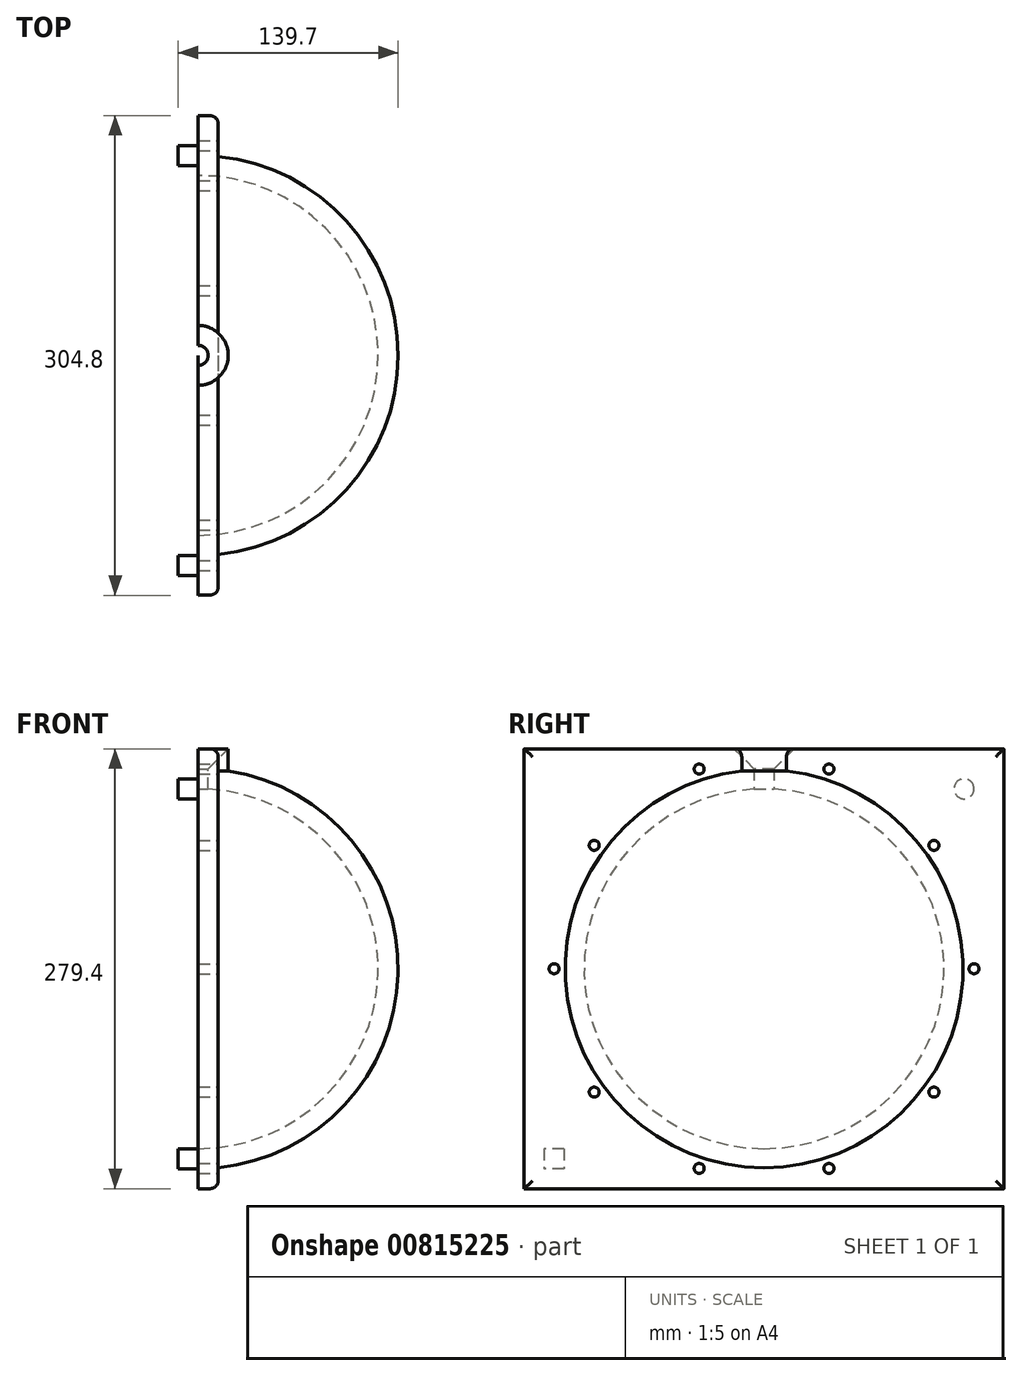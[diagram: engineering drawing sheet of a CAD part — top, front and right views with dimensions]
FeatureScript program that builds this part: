
annotation { "Feature Type Name" : "Feature", "Feature Type Description" : "" }
export const myFeature = defineFeature(function(context is Context, id is Id, definition is map)
    precondition{}
    {
        {
            var Q0;
            Q0=qCreatedBy(makeId("Right.planeOp"),FACE);
            var sketch = newSketch(context, id + "F0", { "sketchPlane" : qUnion([Q0])});
            skCircle(sketch, "E0", {"center": v(0, 0) * mm, "radius": 114.3 * mm});
            skLineSegment(sketch, "E1", {"start": v(0, -114.3) * mm, "end": v(0, -139.7) * mm});
            skLineSegment(sketch, "E2", {"start": v(0, -139.7) * mm, "end": v(152.4, -139.7) * mm});
            skLineSegment(sketch, "E3", {"start": v(152.4, -139.7) * mm, "end": v(152.4, 139.7) * mm});
            skLineSegment(sketch, "E4", {"start": v(152.4, 139.7) * mm, "end": v(6.35, 139.7) * mm});
            skLineSegment(sketch, "E5", {"start": v(6.35, 139.7) * mm, "end": v(6.35, 114.12) * mm});
            skSolve(sketch);
        }
        {
            var Q0;
            {var subQ0=sQuery(id+"F0.wireOp",EDGE,"E1");Q0=makeQuery(id+"F0.imprint","IMPRINT",FACE,{"disambiguationData":[TD([[makeQuery(id+"F0.imprint","IMPRINT",EDGE,{"derivedFrom":subQ0}),1.0]])]});}
            var Q1;
            Q1=sQuery(id+"F0.wireOp",EDGE,"E1");
            revolve(context, id + "F1", {"surfaceOperationType" : NewSurfaceOperationType.NEW, "entities" : qUnion([Q0]), "axis" : qUnion([Q1]), "revolveType" : RevolveType.ONE_DIRECTION, "angle" : 180 * degree});
        }
        {
            var Q0;
            Q0=makeQuery(id+"F1.opRevolve","CAP_FACE",FACE,{"disambiguationData":[OSD([sQuery(id+"F0.wireOp",EDGE,"E0"),sQuery(id+"F0.wireOp",EDGE,"E1"),sQuery(id+"F0.wireOp",EDGE,"E2"),sQuery(id+"F0.wireOp",EDGE,"E3"),sQuery(id+"F0.wireOp",EDGE,"E4"),sQuery(id+"F0.wireOp",EDGE,"E5")])],"isStart":false});
            var sketch = newSketch(context, id + "F2", { "sketchPlane" : qUnion([Q0])});
            skCircle(sketch, "E6", {"center": v(-127, 114.3) * mm, "radius": 6.35 * mm});
            skLineSegment(sketch, "E7.bottom", {"start": v(127, -114.3) * mm, "end": v(139.7, -114.3) * mm});
            skLineSegment(sketch, "E7.top", {"start": v(127, -127) * mm, "end": v(139.7, -127) * mm});
            skLineSegment(sketch, "E7.left", {"start": v(127, -114.3) * mm, "end": v(127, -127) * mm});
            skLineSegment(sketch, "E7.right", {"start": v(139.7, -114.3) * mm, "end": v(139.7, -127) * mm});
            skSolve(sketch);
        }
        {
            var Q0;
            Q0 = qSketchRegion(id + "F2", true);
            extrude(context, id + "F3", {"entities" : qUnion([Q0]), "operationType" : NewBodyOperationType.ADD, "depth" : 12.7 * mm, "offsetDistance" : 25.4 * mm});
        }
        {
            var Q0;
            Q0=makeQuery(id+"F1.opRevolve","SWEPT_FACE",FACE,{"disambiguationData":[OSD([sQuery(id+"F0.wireOp",EDGE,"E3")])]});
            var Q1;
            Q1=makeQuery(id+"F1.opRevolve","SWEPT_FACE",FACE,{"disambiguationData":[OSD([sQuery(id+"F0.wireOp",EDGE,"E4")])]});
            var Q2;
            Q2=makeQuery(id+"F1.opRevolve","SWEPT_FACE",FACE,{"disambiguationData":[OSD([sQuery(id+"F0.wireOp",EDGE,"E2")])]});
            shell(context, id + "F4", {"entities" : qUnion([Q0, Q1, Q2]), "thickness" : 12.7 * mm});
        }
        {
            var Q0;
            Q0=makeQuery(id+"F4.opShell","OFFSET_FACE",FACE,{"disambiguationData":[OSD([sQuery(id+"F0.wireOp",EDGE,"E0"),sQuery(id+"F0.wireOp",EDGE,"E1"),sQuery(id+"F0.wireOp",EDGE,"E2"),sQuery(id+"F0.wireOp",EDGE,"E3"),sQuery(id+"F0.wireOp",EDGE,"E4"),sQuery(id+"F0.wireOp",EDGE,"E5")])]});
            var sketch = newSketch(context, id + "F5", { "sketchPlane" : qUnion([Q0])});
            skArc(sketch, "E8", {"start": v(109.72, 75.8) * mm, "mid": v(107.88, 78.38) * mm, "end": v(105.99, 80.93) * mm});
            skCircle(sketch, "E9", {"center": v(133.35, 0) * mm, "radius": 3.18 * mm});
            skCircle(sketch, "E10.1.0", {"center": v(107.88, 78.38) * mm, "radius": 3.18 * mm});
            skCircle(sketch, "E10.2.0", {"center": v(41.2, 126.82) * mm, "radius": 3.18 * mm});
            skCircle(sketch, "E10.3.0", {"center": v(-41.2, 126.82) * mm, "radius": 3.18 * mm});
            skCircle(sketch, "E10.4.0", {"center": v(-107.88, 78.38) * mm, "radius": 3.18 * mm});
            skCircle(sketch, "E10.5.0", {"center": v(-133.35, 0) * mm, "radius": 3.18 * mm});
            skCircle(sketch, "E10.6.0", {"center": v(-107.88, -78.38) * mm, "radius": 3.18 * mm});
            skCircle(sketch, "E10.7.0", {"center": v(-41.2, -126.82) * mm, "radius": 3.18 * mm});
            skCircle(sketch, "E10.8.0", {"center": v(41.2, -126.82) * mm, "radius": 3.18 * mm});
            skCircle(sketch, "E10.9.0", {"center": v(107.88, -78.38) * mm, "radius": 3.18 * mm});
            skArc(sketch, "E11.trimOffspring", {"start": v(44.22, 125.8) * mm, "mid": v(41.2, 126.82) * mm, "end": v(38.18, 127.77) * mm});
            skArc(sketch, "E12.trimOffspring", {"start": v(133.31, -3.17) * mm, "mid": v(133.35, 0) * mm, "end": v(133.31, 3.17) * mm});
            skArc(sketch, "E13.trimOffspring", {"start": v(-38.18, 127.77) * mm, "mid": v(-41.2, 126.82) * mm, "end": v(-44.22, 125.8) * mm});
            skArc(sketch, "E14.trimOffspring", {"start": v(-105.99, 80.93) * mm, "mid": v(-107.88, 78.38) * mm, "end": v(-109.72, 75.8) * mm});
            skArc(sketch, "E15.trimOffspring", {"start": v(-133.31, 3.17) * mm, "mid": v(-133.35, 0) * mm, "end": v(-133.31, -3.17) * mm});
            skArc(sketch, "E16.trimOffspring", {"start": v(-109.72, -75.8) * mm, "mid": v(-107.88, -78.38) * mm, "end": v(-105.99, -80.93) * mm});
            skArc(sketch, "E17.trimOffspring", {"start": v(-44.22, -125.8) * mm, "mid": v(-41.2, -126.82) * mm, "end": v(-38.18, -127.77) * mm});
            skArc(sketch, "E18.trimOffspring", {"start": v(38.18, -127.77) * mm, "mid": v(41.2, -126.82) * mm, "end": v(44.22, -125.8) * mm});
            skArc(sketch, "E19.trimOffspring", {"start": v(105.99, -80.93) * mm, "mid": v(107.88, -78.38) * mm, "end": v(109.72, -75.8) * mm});
            skSolve(sketch);
        }
        {
            var Q0;
            Q0 = qSketchRegion(id + "F5", true);
            extrude(context, id + "F6", {"entities" : qUnion([Q0]), "operationType" : NewBodyOperationType.REMOVE, "oppositeDirection" : true, "depth" : 25.4 * mm, "offsetDistance" : 25.4 * mm});
        }
        {
            var Q0;
            Q0=makeQuery(id+"F4.opShell","OFFSET_EDGE",EDGE,{"disambiguationData":[OSD([sQuery(id+"F0.wireOp",EDGE,"E2")])]});
            var Q1;
            {var subQ0=sQuery(id+"F0.wireOp",EDGE,"E3");Q1=makeQuery(id+"F4.opShell","OFFSET_EDGE",EDGE,{"disambiguationData":[OSD([subQ0]),TDD([makeQuery(id+"F1.opRevolve","CAP_EDGE",EDGE,{"disambiguationData":[OSD([subQ0])],"isStart":false})])]});}
            var Q2;
            {var subQ0=sQuery(id+"F0.wireOp",EDGE,"E3");Q2=makeQuery(id+"F4.opShell","OFFSET_EDGE",EDGE,{"disambiguationData":[OSD([subQ0]),TDD([makeQuery(id+"F1.opRevolve","CAP_EDGE",EDGE,{"disambiguationData":[OSD([subQ0])],"isStart":true})])]});}
            var Q3;
            {var subQ0=sQuery(id+"F0.wireOp",EDGE,"E4");Q3=makeQuery(id+"F4.opShell","OFFSET_EDGE",EDGE,{"disambiguationData":[OSD([subQ0]),TDD([makeQuery(id+"F1.opRevolve","CAP_EDGE",EDGE,{"disambiguationData":[OSD([subQ0])],"isStart":true})])]});}
            var Q4;
            {var subQ0=sQuery(id+"F0.wireOp",EDGE,"E4");Q4=makeQuery(id+"F4.opShell","OFFSET_EDGE",EDGE,{"disambiguationData":[OSD([subQ0]),TDD([makeQuery(id+"F1.opRevolve","CAP_EDGE",EDGE,{"disambiguationData":[OSD([subQ0])],"isStart":false})])]});}
            fillet(context, id + "F7", {"entities" : qUnion([Q0, Q1, Q2, Q3, Q4]), "radius" : 5.08 * mm, "tangentPropagation" : true, "allowEdgeOverflow" : false});
        }
        {
            var Q0;
            Q0=makeQuery(id+"F1.opRevolve","SWEPT_EDGE",EDGE,{"disambiguationData":[OSD([sQuery(id+"F0.wireOp",EDGE,"E4"),sQuery(id+"F0.wireOp",EDGE,"E5")])]});
            chamfer(context, id + "F8", {"entities" : qUnion([Q0]), "width" : 12.7 * mm, "tangentPropagation" : true});
        }
    });
